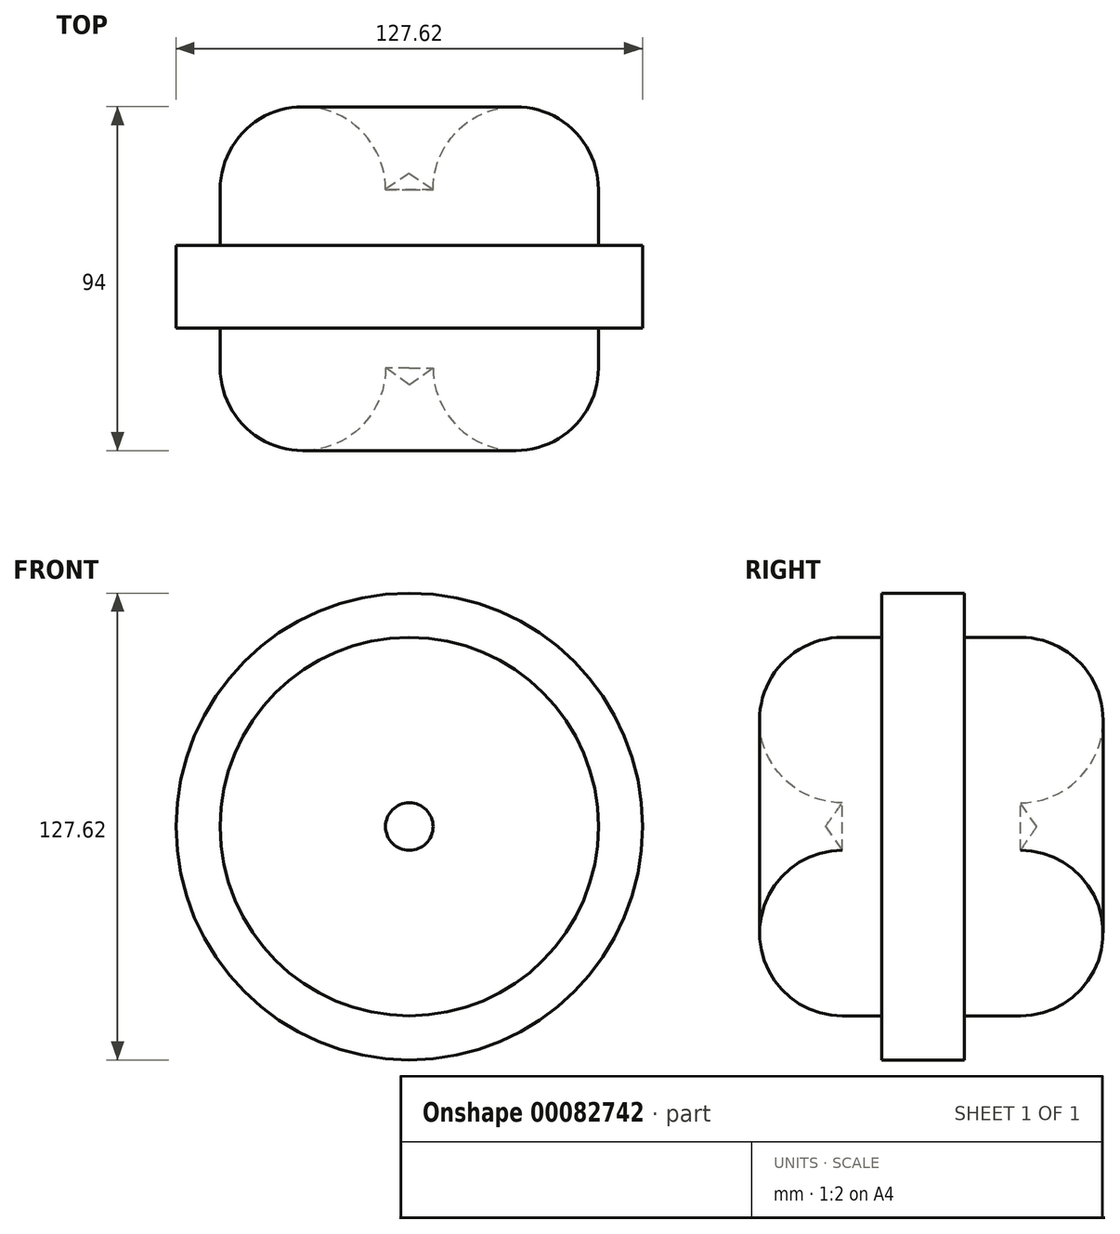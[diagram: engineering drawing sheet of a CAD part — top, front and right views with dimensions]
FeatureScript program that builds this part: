
annotation { "Feature Type Name" : "Feature", "Feature Type Description" : "" }
export const myFeature = defineFeature(function(context is Context, id is Id, definition is map)
    precondition{}
    {
        {
            var Q0;
            Q0=qCreatedBy(makeId("Top.planeOp"),FACE);
            var sketch = newSketch(context, id + "F0", { "sketchPlane" : qUnion([Q0])});
            skLineSegment(sketch, "E0.bottom", {"start": v(-6.5, -24.76) * mm, "end": v(-51.74, -24.76) * mm});
            skLineSegment(sketch, "E0.top", {"start": v(-6.5, 24) * mm, "end": v(-51.74, 24) * mm});
            skLineSegment(sketch, "E0.left", {"start": v(-6.5, -24.76) * mm, "end": v(-6.5, 24) * mm});
            skLineSegment(sketch, "E0.right", {"start": v(-51.74, -24.76) * mm, "end": v(-51.74, 24) * mm});
            skLineSegment(sketch, "E1", {"start": v(-6.5, 24) * mm, "end": v(0, 28.43) * mm});
            skLineSegment(sketch, "E2", {"start": v(-6.5, -24.76) * mm, "end": v(0, -29.34) * mm});
            skArc(sketch, "E3", {"start": v(-6.5, 24) * mm, "mid": v(-29.12, 46.62) * mm, "end": v(-51.74, 24) * mm});
            skArc(sketch, "E4", {"start": v(-51.74, -24.76) * mm, "mid": v(-29.12, -47.38) * mm, "end": v(-6.5, -24.76) * mm});
            skLineSegment(sketch, "E5.bottom", {"start": v(-51.74, 8.71) * mm, "end": v(-63.81, 8.71) * mm});
            skLineSegment(sketch, "E5.top", {"start": v(-51.74, -13.9) * mm, "end": v(-63.81, -13.9) * mm});
            skLineSegment(sketch, "E5.left", {"start": v(-51.74, 8.71) * mm, "end": v(-51.74, -13.9) * mm});
            skLineSegment(sketch, "E5.right", {"start": v(-63.81, 8.71) * mm, "end": v(-63.81, -13.9) * mm});
            skLineSegment(sketch, "E6", {"start": v(0, -29.34) * mm, "end": v(0, 28.43) * mm});
            skSolve(sketch);
        }
        {
            var Q0;
            Q0=makeQuery(id+"F0.imprint","IMPRINT",FACE,{"disambiguationData":[TD([[makeQuery(id+"F0.imprint","IMPRINT",EDGE,{"derivedFrom":sQuery(id+"F0.wireOp",EDGE,"E0.bottom")}),1.0]])]});
            var Q1;
            Q1=makeQuery(id+"F0.imprint","IMPRINT",FACE,{"disambiguationData":[TD([[makeQuery(id+"F0.imprint","IMPRINT",EDGE,{"derivedFrom":sQuery(id+"F0.wireOp",EDGE,"E0.top")}),-1.0]])]});
            var Q2;
            Q2=makeQuery(id+"F0.imprint","IMPRINT",FACE,{"disambiguationData":[TD([[makeQuery(id+"F0.imprint","IMPRINT",EDGE,{"derivedFrom":sQuery(id+"F0.wireOp",EDGE,"E0.left")}),-1.0]])]});
            var Q3;
            Q3=makeQuery(id+"F0.imprint","IMPRINT",FACE,{"disambiguationData":[TD([[makeQuery(id+"F0.imprint","IMPRINT",EDGE,{"derivedFrom":sQuery(id+"F0.wireOp",EDGE,"E5.bottom")}),1.0]])]});
            var Q4;
            {var subQ1=sQuery(id+"F0.wireOp",EDGE,"E0.bottom");Q4=makeQuery(id+"F0.imprint","IMPRINT",FACE,{"disambiguationData":[TD([[makeQuery(id+"F0.imprint","IMPRINT",EDGE,{"derivedFrom":subQ1}),-1.0]])]});}
            var Q5;
            Q5=sQuery(id+"F0.wireOp",EDGE,"E6");
            revolve(context, id + "F1", {"entities" : qUnion([Q0, Q1, Q2, Q3, Q4]), "axis" : qUnion([Q5]), "revolveType" : RevolveType.FULL});
        }
    });
